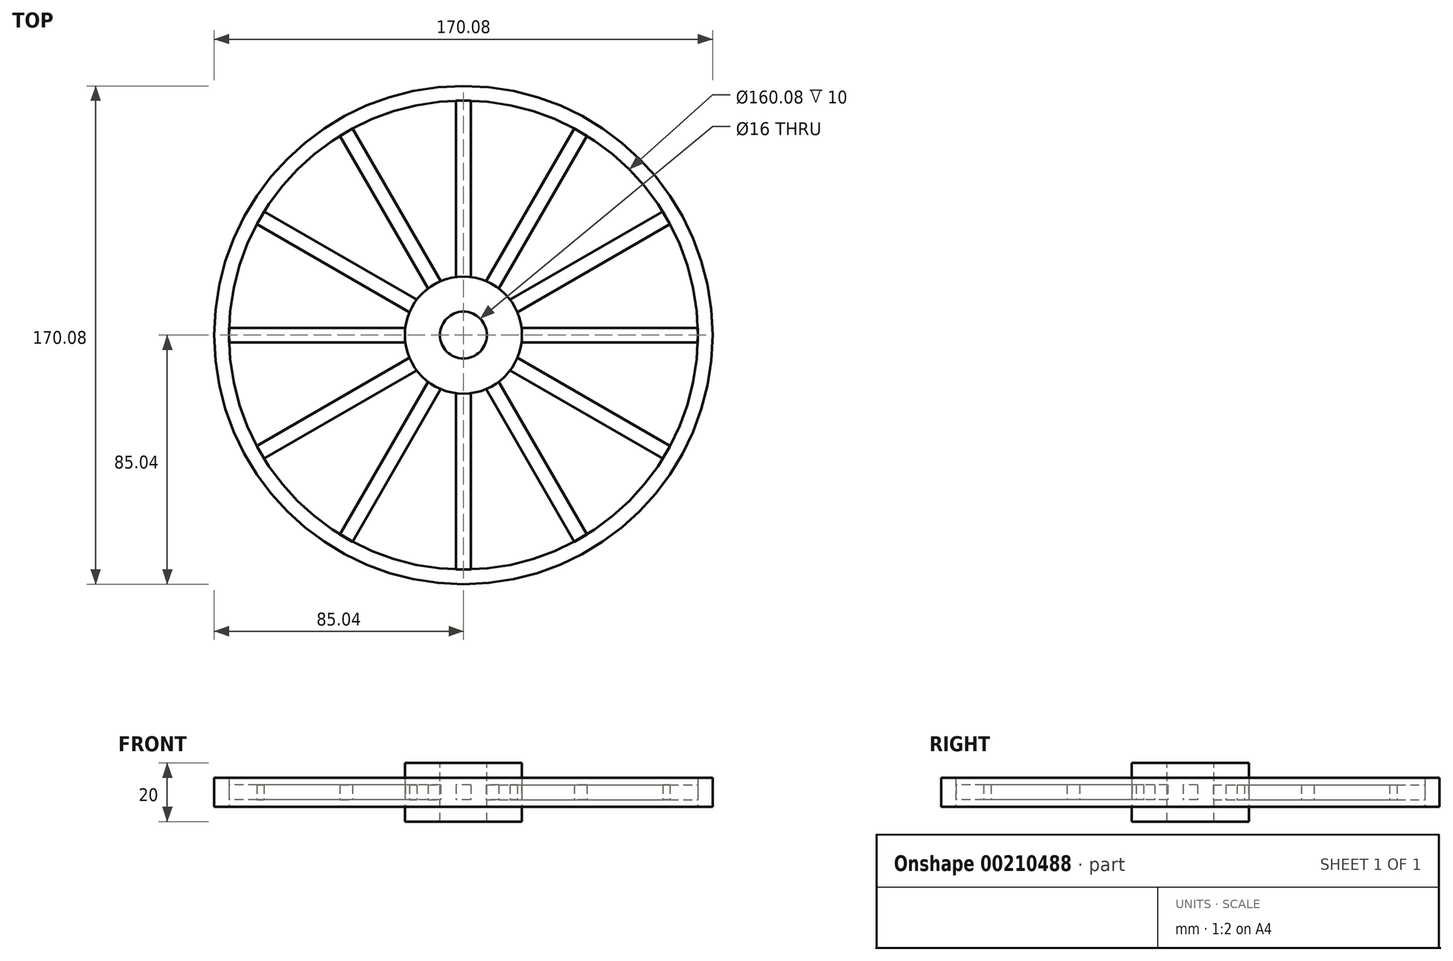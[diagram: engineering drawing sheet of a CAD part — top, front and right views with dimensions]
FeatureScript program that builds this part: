
annotation { "Feature Type Name" : "Feature", "Feature Type Description" : "" }
export const myFeature = defineFeature(function(context is Context, id is Id, definition is map)
    precondition{}
    {
        {
            var Q0;
            Q0=qCreatedBy(makeId("Top.planeOp"),FACE);
            var sketch = newSketch(context, id + "F0", { "sketchPlane" : qUnion([Q0])});
            skCircle(sketch, "E0", {"center": v(0, 0) * mm, "radius": 20 * mm});
            skLineSegment(sketch, "E1.rect.bottom", {"start": v(2.5, 0) * mm, "end": v(-2.5, 0) * mm});
            skLineSegment(sketch, "E1.rect.top", {"start": v(2.5, 80) * mm, "end": v(-2.5, 80) * mm});
            skLineSegment(sketch, "E1.rect.left", {"start": v(2.5, 0) * mm, "end": v(2.5, 80) * mm});
            skLineSegment(sketch, "E1.rect.right", {"start": v(-2.5, 0) * mm, "end": v(-2.5, 80) * mm});
            skPoint(sketch, "E1.rect.middle", {"position": v(0, 40) * mm});
            skCircle(sketch, "E2", {"center": v(0, 0) * mm, "radius": 80.04 * mm});
            skCircle(sketch, "E3.0", {"center": v(0, 0) * mm, "radius": 85.04 * mm});
            skSolve(sketch);
        }
        {
            var Q0;
            {var subQ5=sQuery(id+"F0.wireOp",EDGE,"E1.rect.bottom");Q0=makeQuery(id+"F0.imprint","IMPRINT",FACE,{"disambiguationData":[TD([[makeQuery(id+"F0.imprint","IMPRINT",EDGE,{"derivedFrom":subQ5}),1.0]])]});}
            var Q1;
            {var subQ5=sQuery(id+"F0.wireOp",EDGE,"E1.rect.bottom");Q1=makeQuery(id+"F0.imprint","IMPRINT",FACE,{"disambiguationData":[TD([[makeQuery(id+"F0.imprint","IMPRINT",EDGE,{"derivedFrom":subQ5}),-1.0]])]});}
            extrude(context, id + "F1", {"entities" : qUnion([Q0, Q1]), "depth" : 20 * mm, "symmetric" : true});
        }
        {
            var Q0;
            {var subQ5=sQuery(id+"F0.wireOp",EDGE,"E1.rect.top");Q0=makeQuery(id+"F0.imprint","IMPRINT",FACE,{"disambiguationData":[TD([[makeQuery(id+"F0.imprint","IMPRINT",EDGE,{"derivedFrom":subQ5}),1.0]])]});}
            extrude(context, id + "F2", {"entities" : qUnion([Q0]), "depth" : 5 * mm, "symmetric" : true});
        }
        {
            var Q0;
            Q0=makeQuery(id+"F2.opExtrude","SWEPT_BODY",BODY,{"disambiguationData":[OSD([sQuery(id+"F0.wireOp",EDGE,"E0"),sQuery(id+"F0.wireOp",EDGE,"E1.rect.top"),sQuery(id+"F0.wireOp",EDGE,"E1.rect.left"),sQuery(id+"F0.wireOp",EDGE,"E1.rect.right")])]});
            var Q1;
            Q1=makeQuery(id+"F1.opExtrude","CAP_EDGE",EDGE,{"disambiguationData":[OSD([sQuery(id+"F0.wireOp",EDGE,"E0")])],"isStart":false});
            circularPattern(context, id + "F3", {"entities" : qUnion([Q0]), "axis" : qUnion([Q1]), "angle" : 30 * degree, "instanceCount" : 12, "oppositeDirection" : true});
        }
        {
            var Q0;
            Q0=makeQuery(id+"F0.imprint","IMPRINT",FACE,{"disambiguationData":[TD([[makeQuery(id+"F0.imprint","IMPRINT",EDGE,{"derivedFrom":sQuery(id+"F0.wireOp",EDGE,"E3.0")}),1.0]])]});
            extrude(context, id + "F4", {"entities" : qUnion([Q0]), "depth" : 10 * mm, "symmetric" : true});
        }
        {
            var Q0;
            Q0=qCreatedBy(makeId("Top.planeOp"),FACE);
            var sketch = newSketch(context, id + "F5", { "sketchPlane" : qUnion([Q0])});
            skCircle(sketch, "E4", {"center": v(0, 0) * mm, "radius": 8 * mm});
            skSolve(sketch);
        }
        {
            var Q0;
            Q0=makeQuery(id+"F5.imprint","IMPRINT",FACE,{"disambiguationData":[TD([[makeQuery(id+"F5.imprint","IMPRINT",EDGE,{"derivedFrom":sQuery(id+"F5.wireOp",EDGE,"E4")}),1.0]])]});
            extrude(context, id + "F6", {"entities" : qUnion([Q0]), "operationType" : NewBodyOperationType.REMOVE, "endBound" : BoundingType.THROUGH_ALL, "oppositeDirection" : true, "depth" : 25 * mm, "hasSecondDirection" : true, "secondDirectionOppositeDirection" : false, "secondDirectionDepth" : 25 * mm});
        }
    });
